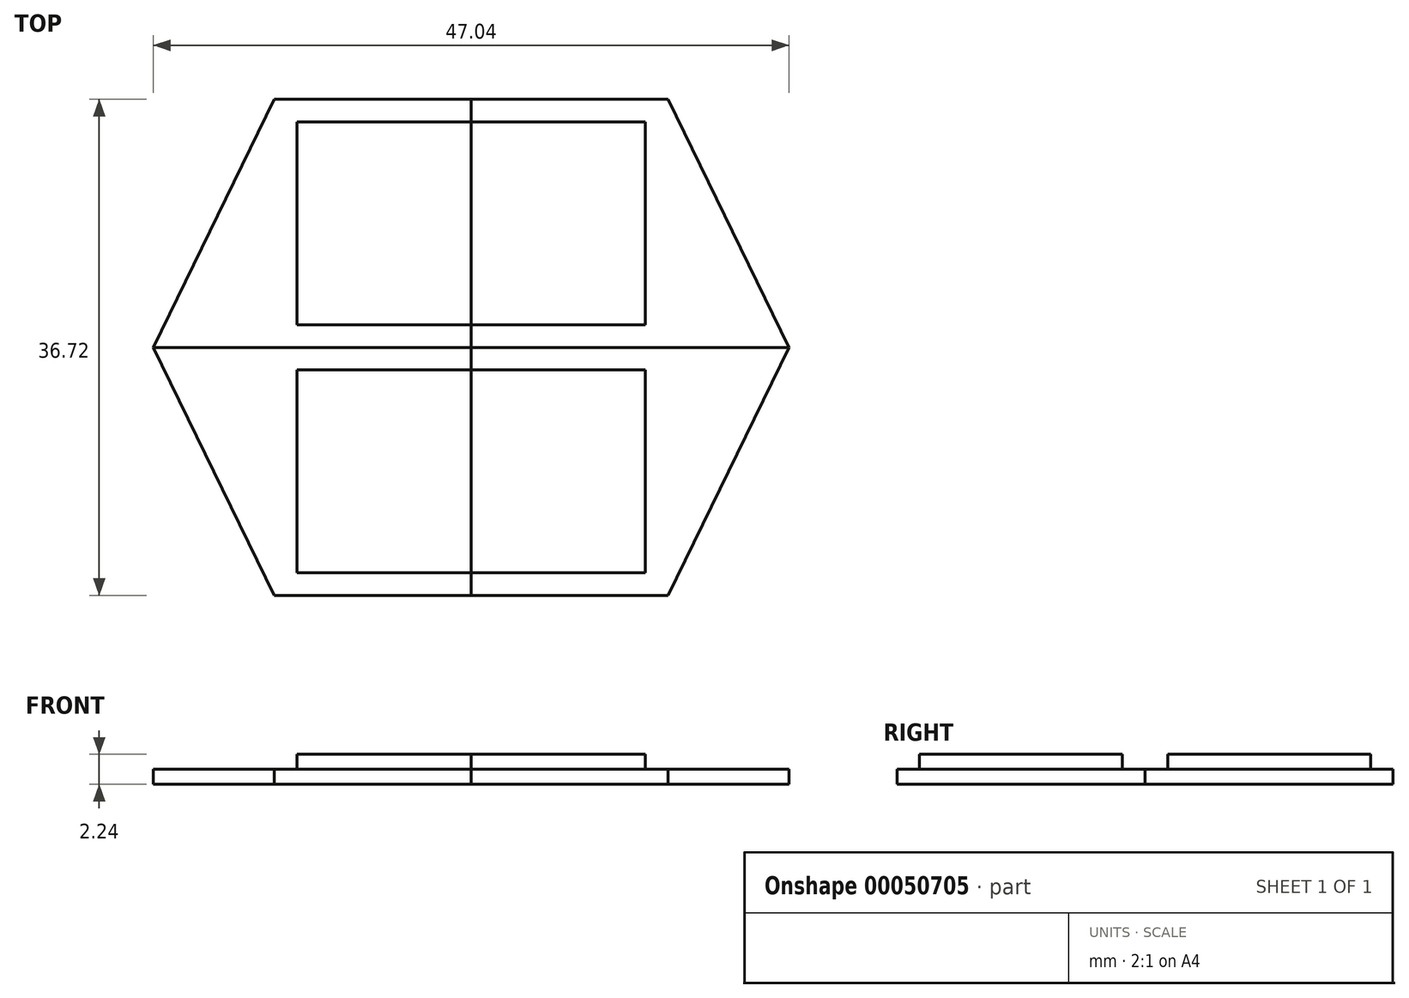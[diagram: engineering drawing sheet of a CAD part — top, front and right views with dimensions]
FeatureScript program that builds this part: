
annotation { "Feature Type Name" : "Feature", "Feature Type Description" : "" }
export const myFeature = defineFeature(function(context is Context, id is Id, definition is map)
    precondition{}
    {
        {
            var Q0;
            Q0=qCreatedBy(makeId("Top.planeOp"),FACE);
            var sketch = newSketch(context, id + "F0", { "sketchPlane" : qUnion([Q0])});
            skLineSegment(sketch, "E0", {"start": v(0, 0) * mm, "end": v(0, 18.36) * mm});
            skLineSegment(sketch, "E1", {"start": v(0, 18.36) * mm, "end": v(14.58, 18.36) * mm});
            skLineSegment(sketch, "E2", {"start": v(14.58, 18.36) * mm, "end": v(23.52, 0) * mm});
            skLineSegment(sketch, "E3", {"start": v(23.52, 0) * mm, "end": v(0, 0) * mm});
            skSolve(sketch);
        }
        {
            var Q0;
            Q0 = qSketchRegion(id + "F0", true);
            extrude(context, id + "F1", {"entities" : qUnion([Q0]), "depth" : 1.12 * mm});
        }
        {
            var Q0;
            Q0=makeQuery(id+"F1.opExtrude","CAP_FACE",FACE,{"disambiguationData":[OSD([sQuery(id+"F0.wireOp",EDGE,"E0"),sQuery(id+"F0.wireOp",EDGE,"E1"),sQuery(id+"F0.wireOp",EDGE,"E2"),sQuery(id+"F0.wireOp",EDGE,"E3")])],"isStart":false});
            var sketch = newSketch(context, id + "F2", { "sketchPlane" : qUnion([Q0])});
            skLineSegment(sketch, "E4", {"start": v(0, 0) * mm, "end": v(0, 1.68) * mm});
            skLineSegment(sketch, "E5", {"start": v(0, 1.68) * mm, "end": v(12.9, 1.68) * mm});
            skLineSegment(sketch, "E6", {"start": v(12.9, 1.68) * mm, "end": v(12.9, 16.69) * mm});
            skLineSegment(sketch, "E7", {"start": v(12.9, 16.69) * mm, "end": v(0, 16.69) * mm});
            skSolve(sketch);
        }
        {
            var Q0;
            {var subQ0=sQuery(id+"F2.wireOp",EDGE,"E5");Q0=makeQuery(id+"F2.imprint","IMPRINT",FACE,{"disambiguationData":[TD([[makeQuery(id+"F2.imprint","IMPRINT",EDGE,{"derivedFrom":subQ0}),1.0]])]});}
            extrude(context, id + "F3", {"entities" : qUnion([Q0]), "operationType" : NewBodyOperationType.ADD, "depth" : 1.12 * mm});
        }
        {
            var Q0;
            Q0=makeQuery(id+"F1.opExtrude","SWEPT_BODY",BODY,{"disambiguationData":[OSD([sQuery(id+"F0.wireOp",EDGE,"E0"),sQuery(id+"F0.wireOp",EDGE,"E1"),sQuery(id+"F0.wireOp",EDGE,"E2"),sQuery(id+"F0.wireOp",EDGE,"E3")])]});
            var Q1;
            {var subQ0=sQuery(id+"F0.wireOp",EDGE,"E0");Q1=makeQuery(id+"F3.boolean.opBoolean","MERGE",FACE,{"derivedFrom":[makeQuery(id+"F1.opExtrude","SWEPT_FACE",FACE,{"disambiguationData":[OSD([subQ0])]}),makeQuery(id+"F3.opExtrude","SWEPT_FACE",FACE,{"disambiguationData":[OSD([subQ0])]})]});}
            mirror(context, id + "F4", {"entities" : qUnion([Q0]), "mirrorPlane" : qUnion([Q1])});
        }
        {
            var Q0;
            Q0=makeQuery(id+"F4.opPattern","COPY",BODY,{"derivedFrom":makeQuery(id+"F1.opExtrude","SWEPT_BODY",BODY,{"disambiguationData":[OSD([sQuery(id+"F0.wireOp",EDGE,"E0"),sQuery(id+"F0.wireOp",EDGE,"E1"),sQuery(id+"F0.wireOp",EDGE,"E2"),sQuery(id+"F0.wireOp",EDGE,"E3")])]}),"instanceName":"1"});
            var Q1;
            Q1=makeQuery(id+"F1.opExtrude","SWEPT_BODY",BODY,{"disambiguationData":[OSD([sQuery(id+"F0.wireOp",EDGE,"E0"),sQuery(id+"F0.wireOp",EDGE,"E1"),sQuery(id+"F0.wireOp",EDGE,"E2"),sQuery(id+"F0.wireOp",EDGE,"E3")])]});
            var Q2;
            Q2=qCreatedBy(makeId("Front.planeOp"),FACE);
            mirror(context, id + "F5", {"entities" : qUnion([Q0, Q1]), "mirrorPlane" : qUnion([Q2])});
        }
    });
